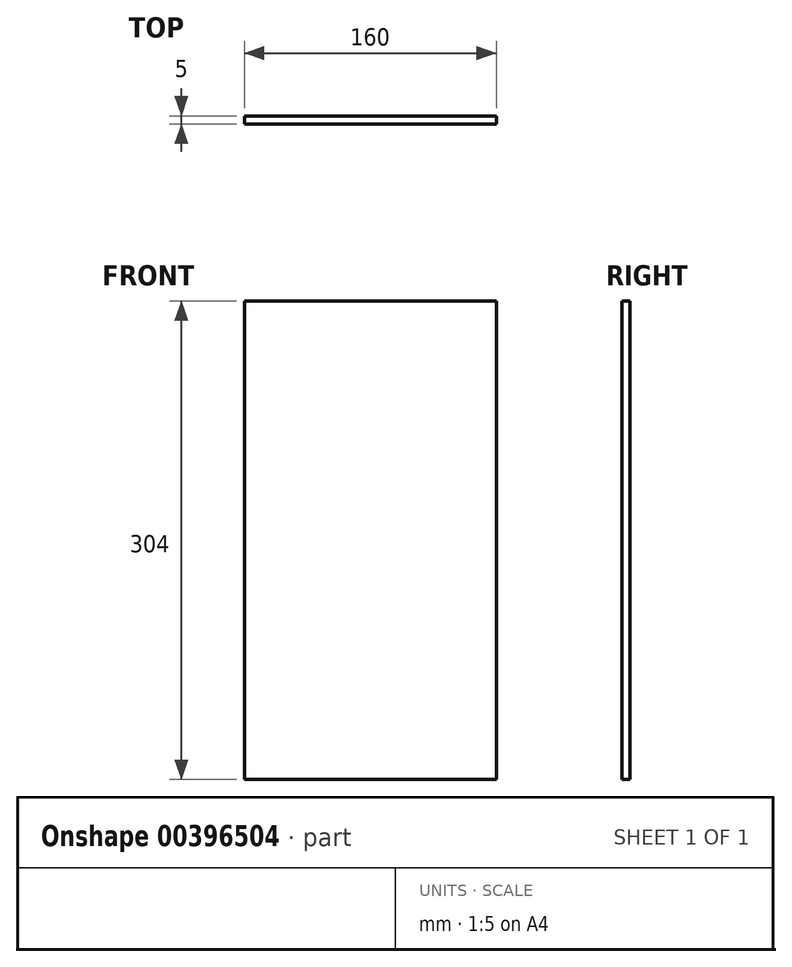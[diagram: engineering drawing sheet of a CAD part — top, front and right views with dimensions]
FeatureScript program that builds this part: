
annotation { "Feature Type Name" : "Feature", "Feature Type Description" : "" }
export const myFeature = defineFeature(function(context is Context, id is Id, definition is map)
    precondition{}
    {
        {
            var Q0;
            Q0=qCreatedBy(makeId("Front.planeOp"),FACE);
            var sketch = newSketch(context, id + "F0", { "sketchPlane" : qUnion([Q0])});
            skLineSegment(sketch, "E0.bottom", {"start": v(-159.26, -126.5) * mm, "end": v(0.74, -126.5) * mm});
            skLineSegment(sketch, "E0.top", {"start": v(-159.26, 177.5) * mm, "end": v(0.74, 177.5) * mm});
            skLineSegment(sketch, "E0.left", {"start": v(-159.26, -126.5) * mm, "end": v(-159.26, 177.5) * mm});
            skLineSegment(sketch, "E0.right", {"start": v(0.74, -126.5) * mm, "end": v(0.74, 177.5) * mm});
            skSolve(sketch);
        }
        {
            var Q0;
            Q0=makeQuery(id+"F0.imprint","IMPRINT",FACE,{"disambiguationData":[TD([[makeQuery(id+"F0.imprint","IMPRINT",EDGE,{"derivedFrom":sQuery(id+"F0.wireOp",EDGE,"E0.bottom")}),1.0]])]});
            extrude(context, id + "F1", {"entities" : qUnion([Q0]), "depth" : 5 * mm});
        }
    });
